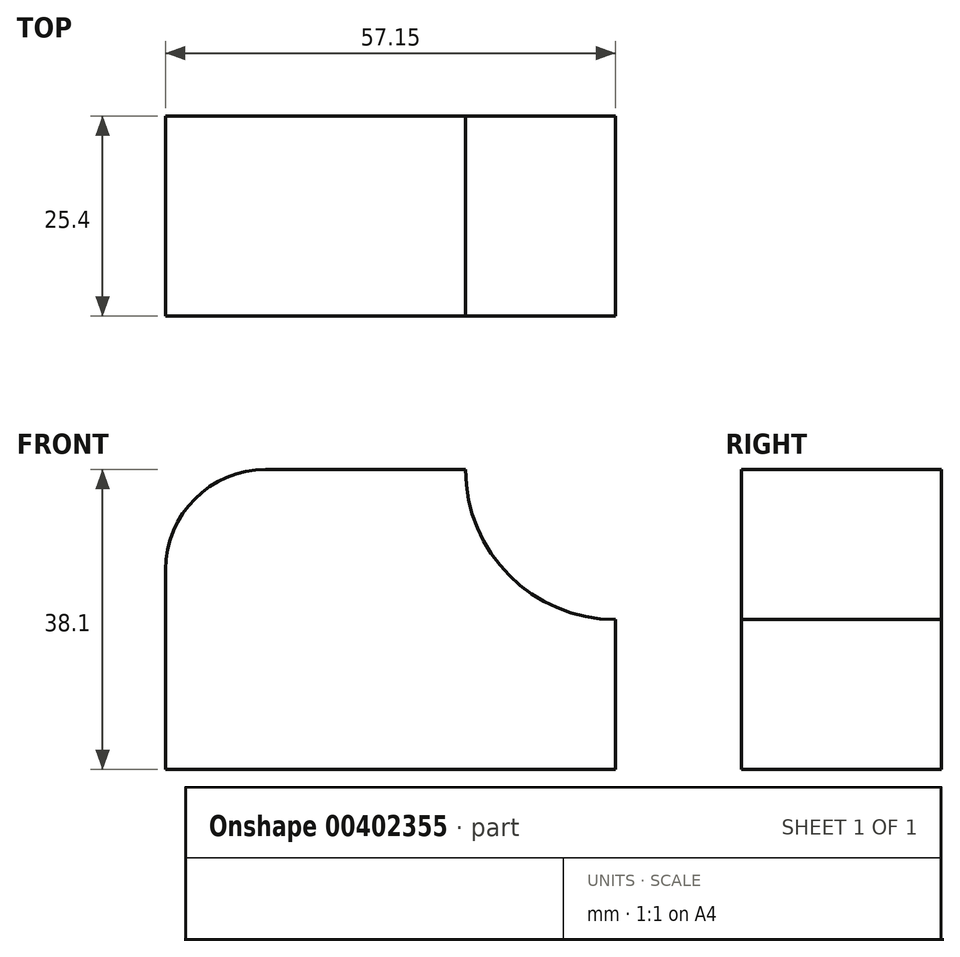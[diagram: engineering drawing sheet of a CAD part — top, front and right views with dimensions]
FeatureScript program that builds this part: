
annotation { "Feature Type Name" : "Feature", "Feature Type Description" : "" }
export const myFeature = defineFeature(function(context is Context, id is Id, definition is map)
    precondition{}
    {
        {
            var Q0;
            Q0=qCreatedBy(makeId("Front.planeOp"),FACE);
            var sketch = newSketch(context, id + "F0", { "sketchPlane" : qUnion([Q0])});
            skLineSegment(sketch, "E0", {"start": v(0, 0) * mm, "end": v(57.15, 0) * mm});
            skLineSegment(sketch, "E1", {"start": v(57.15, 0) * mm, "end": v(57.15, 19.05) * mm});
            skLineSegment(sketch, "E2", {"start": v(0, 0) * mm, "end": v(0, 25.4) * mm});
            skLineSegment(sketch, "E3", {"start": v(12.7, 38.1) * mm, "end": v(38.1, 38.1) * mm});
            skLineSegment(sketch, "E4", {"start": v(57.15, 19.05) * mm, "end": v(38.1, 19.05) * mm});
            skArc(sketch, "E5", {"start": v(12.7, 38.1) * mm, "mid": v(3.72, 34.38) * mm, "end": v(0, 25.4) * mm});
            skArc(sketch, "E6", {"start": v(57.15, 19.05) * mm, "mid": v(43.68, 24.63) * mm, "end": v(38.1, 38.1) * mm});
            skSolve(sketch);
        }
        {
            var Q0;
            Q0=makeQuery(id+"F0.imprint","IMPRINT",FACE,{"disambiguationData":[TD([[makeQuery(id+"F0.imprint","IMPRINT",EDGE,{"derivedFrom":sQuery(id+"F0.wireOp",EDGE,"E0")}),1.0]])]});
            extrude(context, id + "F1", {"entities" : qUnion([Q0]), "depth" : 25.4 * mm});
        }
    });
